# Revit family: Magnuson-Riga-Wate_Receptacle
name_source: partatom
category: Furniture
revit_build: Autodesk Revit 2014 (Build: 20140709_2115(x64)
units: mm (PartAtom-declared; Revit-internal decimal feet)

## types (5) — shared parameters
Assembly Code = E2020200
Body = Stainless Steel, Brushed
Glides = UHMW, Black
Keynote = 12500
Low Emitting Finish = Yes
Low Emitting Material = Yes
Manufacturer = MAGNUSON GROUP
Salvage or Reuse = Yes
Top = UHMW, White
Type Comments = RIGA
URL = www.magnusongroup.com
zero-valued in all types: Percentage of Recycled Content

## per-type parameters (varying)
| type | Depth | Description | Height | Model | Open Front | Open Top | Opn Frnt Dst | Top Open | Width |
| RIGA-10 | 9 3/16" | Stainless Steel Waste Receptacle With Painted Top, 5.3 Gallons | 19 5/16" | RIGA-10 | No | Yes | 1/2" | 4 11/16" | 9 3/16" |
| RIGA-20 | 9 3/16" | Stainless Steel Waste Receptacle With Painted Top, 7.9 Gallons | 27 15/16" | RIGA-20 | No | Yes | 1/2" | 4 11/16" | 9 3/16" |
| RIGA-30 | 12 3/16" | Stainless Steel Waste Receptacle With Painted Top, 13.2 Gallons | 28 3/4" | RIGA-30 | No | Yes | 1/2" | 6 7/8" | 12 3/16" |
| RIGA-40 | 13 3/4" | Stainless Steel Waste Receptacle With Painted Top, 23.8 Gallons | 29 15/16" | RIGA-40 | No | Yes | 1/2" | 6 7/8" | 13 3/4" |
| RIGA-ASH | 9 13/16" | Stainless Steel Waste Receptacle With Painted Top, 23.8 Gallons | 27 15/16" | RIGA-40 | Yes | No | 2" | 5" | 9 13/16" |

## geometry (parser evidence)
native form markers: Sweep x2
no freeform markers — native parametric forms only
